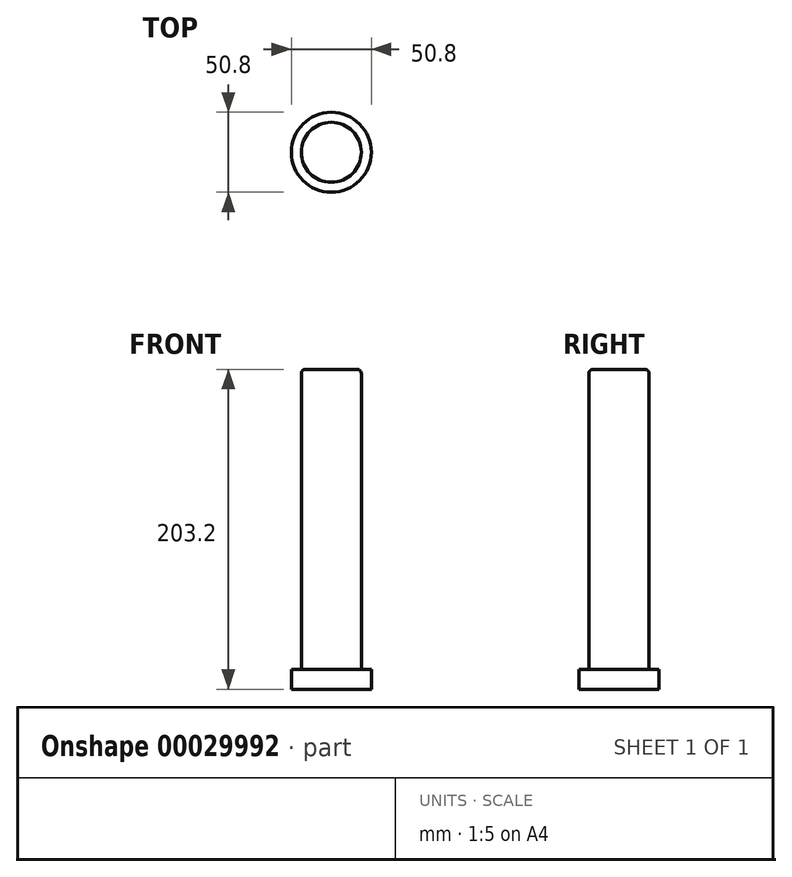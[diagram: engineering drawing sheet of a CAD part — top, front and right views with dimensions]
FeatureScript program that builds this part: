
annotation { "Feature Type Name" : "Feature", "Feature Type Description" : "" }
export const myFeature = defineFeature(function(context is Context, id is Id, definition is map)
    precondition{}
    {
        {
            var Q0;
            Q0=qCreatedBy(makeId("Top.planeOp"),FACE);
            var sketch = newSketch(context, id + "F0", { "sketchPlane" : qUnion([Q0])});
            skCircle(sketch, "E0", {"center": v(0, 0) * mm, "radius": 25.4 * mm});
            skSolve(sketch);
        }
        {
            var Q0;
            Q0=makeQuery(id+"F0.imprint","IMPRINT",FACE,{"disambiguationData":[TD([[makeQuery(id+"F0.imprint","IMPRINT",EDGE,{"derivedFrom":sQuery(id+"F0.wireOp",EDGE,"E0")}),1.0]])]});
            extrude(context, id + "F1", {"entities" : qUnion([Q0]), "depth" : 12.7 * mm});
        }
        {
            var Q0;
            Q0=makeQuery(id+"F1.opExtrude","CAP_FACE",FACE,{"disambiguationData":[OSD([sQuery(id+"F0.wireOp",EDGE,"E0")])],"isStart":false});
            var sketch = newSketch(context, id + "F2", { "sketchPlane" : qUnion([Q0])});
            skCircle(sketch, "E1.0", {"center": v(0, 0) * mm, "radius": 25.4 * mm, "construction": true});
            skCircle(sketch, "E2", {"center": v(0, 0) * mm, "radius": 19.05 * mm});
            skSolve(sketch);
        }
        {
            var Q0;
            Q0=makeQuery(id+"F2.imprint","IMPRINT",FACE,{"disambiguationData":[TD([[makeQuery(id+"F2.imprint","IMPRINT",EDGE,{"derivedFrom":sQuery(id+"F2.wireOp",EDGE,"E2")}),1.0]])]});
            extrude(context, id + "F3", {"entities" : qUnion([Q0]), "operationType" : NewBodyOperationType.ADD, "depth" : 190.5 * mm});
        }
        {
            var Q0;
            Q0=makeQuery(id+"F3.opExtrude","CAP_FACE",FACE,{"disambiguationData":[OSD([sQuery(id+"F2.wireOp",EDGE,"E2")])],"isStart":false});
            fillet(context, id + "F4", {"entities" : qUnion([Q0]), "radius" : 2.54 * mm, "tangentPropagation" : true, "allowEdgeOverflow" : false});
        }
    });
